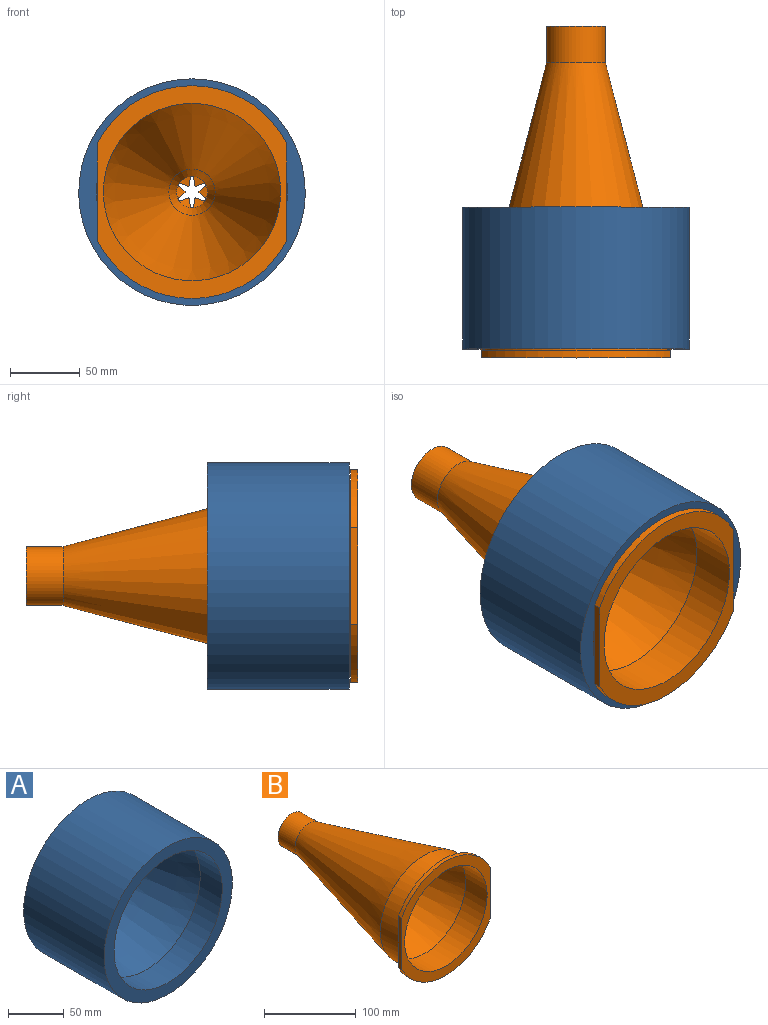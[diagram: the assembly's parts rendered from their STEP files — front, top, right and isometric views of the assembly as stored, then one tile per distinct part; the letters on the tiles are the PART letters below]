
ASSEMBLY  parts=2 mates=1
PART A: 6 faces, bbox 162.3x101.6x162.3 mm
  f0: cylinder r=50.42mm len=100.84mm, axis (0,1,0), area 2333.5mm2, adj f1,f5
  f1: plane 162.26x162.26mm, normal (0,1,0), area 12690.8mm2, adj f0,f2
  f2: cylinder r=81.13mm len=162.26mm, axis (0,1,0), area 51789.6mm2, adj f1,f3
  f3: plane 162.26x162.26mm, normal (0,-1,0), area 5967mm2, adj f2,f4
  f4: cylinder r=68.43mm len=136.86mm, axis (0,1,0), area 12012.6mm2, adj f3,f5
  f5: cone r=68.43mm half-angle=15.2deg, axis (0,-1,0), area 25649mm2, adj f0,f4
PART B: 44 faces, bbox 135.9x237.6x152.4 mm
  f0: cone r=11.18mm half-angle=78.5deg, axis (0,-1,0), area 33.7mm2, adj f7,f23,f27,f28,f41,f42
  f1: cone r=11.18mm half-angle=78.5deg, axis (0,-1,0), area 33.7mm2, adj f12,f23,f38,f40,f41,f43
  f2: cone r=11.18mm half-angle=78.5deg, axis (0,-1,0), area 33.7mm2, adj f11,f23,f35,f37,f39,f40
  f3: cone r=11.18mm half-angle=78.5deg, axis (0,-1,0), area 33.7mm2, adj f10,f23,f32,f34,f36,f37
  f4: cone r=11.18mm half-angle=78.5deg, axis (0,-1,0), area 33.7mm2, adj f9,f23,f30,f31,f33,f34
  f5: cone r=11.18mm half-angle=78.5deg, axis (0,-1,0), area 33.7mm2, adj f8,f23,f26,f28,f29,f30
  f6: plane 42.16x42.16mm, normal (0,1,0), area 1201.7mm2, adj f7,f8,f9,f10,f11,f12,f18,f26
  f7: cylinder r=4.95mm len=6.35mm, axis (0,1,0), area 4.9mm2, adj f0,f6,f27,f42
  f8: cylinder r=4.95mm len=6.35mm, axis (0,1,0), area 4.9mm2, adj f5,f6,f26,f29
  f9: cylinder r=4.95mm len=6.35mm, axis (0,1,0), area 4.9mm2, adj f4,f6,f31,f33
  f10: cylinder r=4.95mm len=6.35mm, axis (0,1,0), area 4.9mm2, adj f3,f6,f32,f36
  f11: cylinder r=4.95mm len=6.35mm, axis (0,1,0), area 4.9mm2, adj f2,f6,f35,f39
  f12: cylinder r=4.95mm len=6.35mm, axis (0,1,0), area 4.9mm2, adj f1,f6,f38,f43
  f13: plane 135.89x76.2mm, normal (0,1,0), area 1485.1mm2, adj f15,f20,f24,f25
  f14: plane 135.89x76.2mm, normal (0,1,0), area 1485.1mm2, adj f16,f20,f24,f25
  f15: cylinder r=76.2mm len=135.89mm, axis (0,1,0), area 852.4mm2, adj f13,f17,f24,f25
  f16: cylinder r=76.2mm len=135.89mm, axis (0,1,0), area 852.4mm2, adj f14,f17,f24,f25
  f17: plane 152.4x135.89mm, normal (0,-1,0), area 4805.8mm2, adj f15,f16,f21,f24,f25
  f18: cylinder r=21.08mm len=42.16mm, axis (0,1,0), area 3499.1mm2, adj f6,f19
  f19: cone r=21.08mm half-angle=14.7deg, axis (0,-1,0), area 51522.8mm2, adj f18,f20
  f20: cylinder r=67.95mm len=135.89mm, axis (0,1,0), area 11927.9mm2, adj f13,f14,f19
  f21: cylinder r=63.5mm len=127mm, axis (0,1,0), area 13174.4mm2, adj f17,f22
  f22: cone r=63.5mm half-angle=14.7deg, axis (0,-1,0), area 46377.8mm2, adj f21,f23
  f23: cone r=16.64mm half-angle=16.2deg, axis (0,-1,0), area 1710.3mm2, adj f0,f1,f2,f3,f4,f5,f22
  f24: plane 68.99x5.08mm, normal (1,0,0), area 350.5mm2, adj f13,f14,f15,f16,f17
  f25: plane 68.99x5.08mm, normal (-1,0,0), area 350.5mm2, adj f13,f14,f15,f16,f17
  f26: plane 7.36x5.07mm, normal (0.35,0,-0.93), area 37.1mm2, adj f5,f6,f8,f28
  f27: plane 7.36x4.2mm, normal (-0.63,0,0.77), area 37.1mm2, adj f0,f6,f7,f28
  f28: cylinder r=1.27mm len=7.62mm, axis (0,1,0), area 31.1mm2, adj f0,f5,f6,f26,f27
  f29: plane 7.36x5.36mm, normal (-0.99,0,-0.16), area 37.1mm2, adj f5,f6,f8,f30
  f30: cylinder r=1.27mm len=7.62mm, axis (0,1,0), area 31.1mm2, adj f4,f5,f6,f29,f31
  f31: plane 7.36x5.36mm, normal (0.99,0,-0.16), area 37.1mm2, adj f4,f6,f9,f30
  f32: plane 7.36x4.2mm, normal (0.63,0,0.77), area 37.1mm2, adj f3,f6,f10,f34
  f33: plane 7.36x5.07mm, normal (-0.35,0,-0.93), area 37.1mm2, adj f4,f6,f9,f34
  f34: cylinder r=1.27mm len=7.62mm, axis (0,1,0), area 31.1mm2, adj f3,f4,f6,f32,f33
  f35: plane 7.36x5.07mm, normal (-0.35,0,0.93), area 37.1mm2, adj f2,f6,f11,f37
  f36: plane 7.36x4.2mm, normal (0.63,0,-0.77), area 37.1mm2, adj f3,f6,f10,f37
  f37: cylinder r=1.27mm len=7.62mm, axis (0,1,0), area 31.1mm2, adj f2,f3,f6,f35,f36
  f38: plane 7.36x5.36mm, normal (-0.99,0,0.16), area 37.1mm2, adj f1,f6,f12,f40
  f39: plane 7.36x5.36mm, normal (0.99,0,0.16), area 37.1mm2, adj f2,f6,f11,f40
  f40: cylinder r=1.27mm len=7.62mm, axis (0,1,0), area 31.1mm2, adj f1,f2,f6,f38,f39
  f41: cylinder r=1.27mm len=7.62mm, axis (0,1,0), area 31.1mm2, adj f0,f1,f6,f42,f43
  f42: plane 7.36x4.2mm, normal (-0.63,0,-0.77), area 37.1mm2, adj f0,f6,f7,f41
  f43: plane 7.36x5.07mm, normal (0.35,0,0.93), area 37.1mm2, adj f1,f6,f12,f41
PLACE A t=(0,-129.72,0)mm
PLACE B at identity fixed
MATE slider B.f0 <-> A.f0  axis (0,1,0) through (0,-218.54,0)mm
